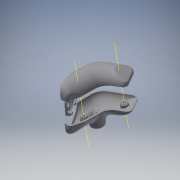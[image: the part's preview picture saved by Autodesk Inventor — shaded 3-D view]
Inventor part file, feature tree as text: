
AUTODESK INVENTOR PART (.ipt)
format: ipt  version: 2016 (Build 200138000, 138)  size: 18,297,344 bytes
history: native  units: in
note: dims shown in document units (in); Inventor stores cm internally (conversion verified against a paired STEP export)
features: sketch x44, other x39, extrude x33, surface_op x32, fillet x22, draft x19, plane x18, chamfer x18, move_body x12, projected_geometry x10, loft x4, shell x4, boolean_combine x2, split x2, delete_face x1
ambient origin geometry x8: Origin, YZ Plane, XZ Plane, XY Plane, X Axis, Y Axis, Z Axis, Center Point
bodies: Solid1 (feature_tree), Solid2 (feature_tree), Solid5 (feature_tree), Solid8 (feature_tree), Solid9 (feature_tree), Solid10 (feature_tree), Solid6 (feature_tree), Solid7 (feature_tree), Solid12 (feature_tree), Solid13 (feature_tree)
feature tree (260):
  sketch  "Sketch1"  dims[d0=0.7in d1=0.6in]
  plane  "Work Plane1"
  sketch  "Sketch2"  dims[d2=2.0in d3=0.73in]
  loft  "Loft1"
  plane  "Work Plane3"
  plane  "Work Plane4"
  plane  "Work Plane6"
  delete_face  "Delete Face1"
  surface_op  "Extend1"
  sketch  "Sketch6"  dims[d4=0.68in d5=120.0deg d6=0.8125in d9=0.75in]
  surface_op  "Stitch Surface1"
  extrude  "Extrusion5"  Depth=2.0in
  extrude  "Extrusion6"  Depth=0.8125in TaperAngle=120.0deg
  boolean_combine  "Combine1"
  extrude  "Extrusion7"  TaperAngle=0.0deg  [1 undecoded]
  loft  "Loft5"
  fillet  "Fillet6"  Radius=1.0in
  fillet  "Fillet7"  Radius=0.1969in
  plane  "Work Plane7"
  plane  "Work Plane8"
  extrude  "Extrusion10"  Depth=0.1969in
  draft  "FaceDraft1"
  fillet  "Fillet15"  [1 undecoded]
  extrude  "Extrusion15"  TaperAngle=90.0deg  [1 undecoded]
  fillet  "Fillet19"  Radius=0.35in
  fillet  "Fillet20"  [1 undecoded]
  extrude  "Extrusion9"  Depth=0.1in
  fillet  "Fillet11"  Radius=0.0687in
  fillet  "Fillet22"  Radius=0.75in
  shell  "Shell1"  Thickness=0.875in
  extrude  "Extrusion16"  Depth=0.3937in
  extrude  "Extrusion11"  Depth=0.141in
  draft  "FaceDraft5"
  sketch  "3D Sketch2"
  plane  "Work Plane9"
  extrude  "Extrusion17"  Depth=0.3125in TaperAngle=0.0deg
  plane  "Work Plane10"
  extrude  "Extrusion18"  Depth=0.0172in
  plane  "Work Plane11"
  extrude  "Extrusion19"  Depth=0.225in
  plane  "Work Plane12"
  extrude  "Extrusion20"  Depth=0.13in
  draft  "FaceDraft2"
  draft  "FaceDraft3"
  extrude  "Extrusion21"  Depth=0.4in
  extrude  "Extrusion22"  [1 undecoded]
  sketch  "Sketch25"  dims[d130=-0.625in d131=0.4in]
  extrude  "Extrusion23"  Depth=1.0in TaperAngle=0.0deg
  extrude  "Extrusion24"  Depth=0.28in
  extrude  "Extrusion25"  [1 undecoded]
  draft  "FaceDraft4"
  extrude  "Extrusion26"  Depth=1.0in TaperAngle=0.0deg
  plane  "Work Plane13"
  sketch  "Sketch29"  dims[d140=1.0in d141=0.0in d142=-0.06in]
  plane  "Work Plane14"
  sketch  "Sketch30"  dims[d143=0.28in d144=1.0in d145=0.0in]
  surface_op  "Stitch Surface5"
  surface_op  "Extend3"
  surface_op  "Extend4"
  surface_op  "Stitch Surface6"
  sketch  "Sketch35"  dims[d151=0.13in d152=1.0in d153=0.0in]
  surface_op  "Stitch Surface7"
  split  "Split2"
  sketch  "Sketch39"  dims[d160=0.06in d161=1.0in d162=0.0in]
  extrude  "Extrusion27"  Depth=0.0206in
  chamfer  "Chamfer4"  Distance=1.0in
  chamfer  "Chamfer5"  Distance=1.0in
  chamfer  "Chamfer6"  Distance=1.0in
  chamfer  "Chamfer7"  Distance=1.0in
  chamfer  "Chamfer9"  Distance=1.0in
  chamfer  "Chamfer10"  Distance=1.0in
  chamfer  "Chamfer11"  Distance=0.1969in
  chamfer  "Chamfer16"  [1 undecoded]
  chamfer  "Chamfer17"  [1 undecoded]
  chamfer  "Chamfer12"  [1 undecoded]
  chamfer  "Chamfer18"  [1 undecoded]
  chamfer  "Chamfer19"  [1 undecoded]
  chamfer  "Chamfer20"  [1 undecoded]
  chamfer  "Chamfer21"  [1 undecoded]
  chamfer  "Chamfer22"  [1 undecoded]
  chamfer  "Chamfer23"  [1 undecoded]
  chamfer  "Chamfer24"  Distance=0.1969in
  chamfer  "Chamfer25"  [1 undecoded]
  extrude  "Extrusion29"  Depth=0.02in
  draft  "FaceDraft6"
  fillet  "Fillet26"  Radius=0.02in
  move_body  "Move Body2"
  move_body  "Move Body3"
  draft  "FaceDraft7"
  draft  "FaceDraft8"
  draft  "FaceDraft9"
  draft  "FaceDraft10"
  extrude  "Extrusion30"  TaperAngle=0.0deg  [1 undecoded]
  draft  "FaceDraft16"
  draft  "FaceDraft17"
  extrude  "Extrusion31"  Depth=0.1969in TaperAngle=0.0deg
  extrude  "Extrusion32"  TaperAngle=0.0deg  [1 undecoded]
  extrude  "Extrusion33"  Depth=0.1969in
  draft  "FaceDraft18"
  draft  "FaceDraft19"
  draft  "FaceDraft20"
  fillet  "Fillet28"  Radius=0.1969in
  extrude  "Extrusion34"  TaperAngle=0.0deg  [1 undecoded]
  extrude  "Extrusion35"  Depth=0.1969in
  extrude  "Extrusion36"  Depth=0.5in
  draft  "FaceDraft21"
  draft  "FaceDraft22"
  draft  "FaceDraft23"
  shell  "Shell2"  Thickness=0.35in
  shell  "Shell3"  Thickness=0.125in
  shell  "Shell4"  Thickness=0.05in
  fillet  "Fillet32"  Radius=0.05in
  fillet  "Fillet29"  Radius=0.05in
  fillet  "Fillet30"  Radius=0.05in
  fillet  "Fillet31"  Radius=0.05in
  fillet  "Fillet33"  Radius=0.05in
  extrude  "Extrusion40"  Depth=0.05in
  draft  "FaceDraft26"
  fillet  "Fillet44"  Radius=0.05in
  fillet  "Fillet39"  Radius=0.05in
  move_body  "Move Body4"
  fillet  "Fillet45"  Radius=0.05in
  fillet  "Fillet46"  Radius=0.05in
  fillet  "Fillet37"  Radius=0.05in
  fillet  "Fillet48"  Radius=0.05in
  fillet  "Fillet49"  Radius=0.05in
  fillet  "Fillet50"  Radius=0.05in
  sketch  "Sketch57"  dims[d172=0.0in]
  sketch  "Sketch60"  dims[d173=0.1969in]
  other  "Work Point1"
  other  "Work Point2"
  other  "Work Point3"
  plane  "Work Plane17"
  move_body  "Move Body5"
  move_body  "Move Body6"
  move_body  "Move Body7"
  move_body  "Move Body8"
  other  "Work Axis1"
  other  "Work Axis2"
  boolean_combine  "Combine2"
  split  "Split3"
  loft  "Loft6"
  loft  "Loft7"
  move_body  "Move Body10"
  move_body  "Move Body11"
  move_body  "Move Body12"
  move_body  "Move Body13"
  move_body  "Move Body14"
  sketch  "Sketch61"  dims[d174=0.0in]
  plane  "Work Plane18"
  extrude  "Extrusion46"  Depth=0.05in
  sketch  "3D Sketch3"
  plane  "Work Plane19"
  extrude  "Extrusion47"  Depth=0.05in
  sketch  "Sketch63"  dims[d176=0.1969in]
  plane  "Work Plane20"
  extrude  "Extrusion48"  Depth=0.0508in
  extrude  "Extrusion49"  Depth=0.05in
  extrude  "Extrusion50"  Depth=0.05in TaperAngle=0.0deg
  plane  "Work Plane2"
  plane  "Work Plane5"
  other  "Srf1"
  other  "Srf2"
  sketch  "Sketch8"  dims[d10=0.0in d11=90.0deg d12=0.0in d13=90.0deg]
  sketch  "Sketch9"  dims[d14=150.0deg d15=-0.5in d45=1.0in d46=0.0in d47=1.0in d48=0.0in d49=0.1969in]
  sketch  "Sketch11"  dims[d50=0.0in d51=0.1969in d52=0.0in]
  sketch  "Sketch12"  dims[d53=1.0in d54=0.0in d56=90.0deg d58=90.0deg]
  other  "Edges5"
  other  "Edges6"
  sketch  "Sketch13"  dims[d62=0.0in d63=90.0deg d64=0.0in d65=90.0deg d66=0.2875in d67=0.35in d78=90.0deg]
  sketch  "Sketch17"  dims[d79=1.0in d80=0.0in d81=0.1in d87=0.0687in d88=0.75in d89=0.875in d90=0.0in]
  sketch  "Sketch18"  dims[d92=0.3937in d93=0.3937in]
  projected_geometry  "Projected Loop3"
  other  "Silhouette Curve2"
  sketch  "Sketch19"  dims[d94=0.2625in d95=0.141in]
  sketch  "Sketch20"  dims[d96=0.5in d97=0.3125in d98=0.0in]
  sketch  "Sketch21"  dims[d107=0.1in d114=0.0172in]
  sketch  "Sketch22"  dims[d117=0.121in d118=0.0in]
  sketch  "Sketch23"  dims[d119=0.1in d120=0.1in d121=0.13in d122=0.1969in d123=0.3in d124=0.2169in d125=0.225in]
  sketch  "Sketch24"  dims[d126=0.15in d127=0.0in d129=0.13in]
  sketch  "Sketch26"  dims[d132=1.0in d133=0.0in d134=-0.875in]
  sketch  "Sketch27"  dims[d135=0.4in d136=1.0in d137=0.0in]
  sketch  "Sketch28"  dims[d138=-0.06in d139=0.28in]
  other  "Srf3"
  other  "Srf4"
  other  "Srf5"
  other  "Srf6"
  other  "Srf7"
  other  "Srf8"
  other  "Srf12"
  other  "Srf13"
  other  "Srf15"
  other  "Srf17"
  other  "Srf18"
  other  "Srf19"
  other  "Srf21"
  other  "Srf24"
  other  "Srf25"
  sketch  "Sketch33"  dims[d146=0.0206in d147=0.0206in]
  sketch  "Sketch34"  dims[d148=0.13in d149=1.0in d150=0.0in]
  other  "Srf28"
  other  "Srf30"
  other  "Srf31"
  other  "Srf32"
  other  "Srf33"
  other  "Srf34"
  other  "Srf35"
  sketch  "Sketch36"  dims[d154=0.06in]
  other  "Srf36"
  other  "Srf37"
  other  "Srf38"
  sketch  "Sketch37"  dims[d155=0.06in d156=1.0in d157=0.0in d158=1.0in d159=0.0in]
  sketch  "Sketch41"  dims[d163=0.0206in]
  sketch  "Sketch43"  dims[d164=0.23in d165=1.0in d166=0.0in]
  sketch  "Sketch44"  dims[d167=15.0deg]
  sketch  "Sketch45"  dims[d168=0.125in]
  sketch  "Sketch46"  dims[d169=0.125in]
  sketch  "Sketch47"  dims[d170=0.0in]
  projected_geometry  "Projected Loop4"
  projected_geometry  "Projected Loop5"
  sketch  "Sketch51"  dims[d171=0.1969in]
  projected_geometry  "Projected Loop13"
  other  "Edges7"
  other  "Edges8"
  other  "Edges9"
  other  "Edges10"
  projected_geometry  "Projected Loop14"
  sketch  "Sketch62"  dims[d175=0.0in]
  projected_geometry  "Projected Loop15"
  projected_geometry  "Projected Loop16"
  sketch  "Sketch65"  dims[d177=0.0in d178=0.1969in d179=0.0in]
  sketch  "Sketch66"  dims[d184=0.0in d185=0.0in d187=0.0in d191=0.0in d192=0.0in d193=0.0in d197=0.0in d201=0.0in d204=0.0in d208=0.0in d209=0.1969in d210=0.0in d212=0.02in d213=0.02in d214=0.0in d216=0.1969in d217=0.1969in d218=0.0in d219=0.0in d220=0.1969in d221=0.1969in d222=0.0in d223=0.1969in d227=0.5in d228=0.35in d229=0.125in d233=0.05in d234=0.05in d235=0.0in d236=0.05in d237=0.125in d238=0.1374in d239=0.05in d240=0.125in d241=0.1374in d242=0.05in d243=0.125in d244=0.1374in d245=0.05in d246=0.125in d247=0.1374in d251=0.05in d252=0.125in d253=0.0687in d254=0.05in d255=0.125in d256=0.0687in d257=0.05in d258=0.125in d259=0.0687in d260=0.05in d261=0.125in d262=0.0687in d272=0.05in d273=0.125in d274=0.0687in d275=0.05in d276=0.125in d277=0.0687in d278=0.05in d279=0.125in d280=0.0687in d281=0.05in d282=0.125in d283=0.0687in d284=0.05in d285=0.125in d286=0.0687in d287=0.05in d288=0.125in d289=0.0687in d290=0.05in d291=0.125in d292=0.0687in d293=0.05in d294=0.125in d295=0.0687in d296=0.05in d297=0.125in d298=0.0687in d299=0.0508in d300=0.125in d301=0.0687in d302=0.05in d308=0.05in d309=0.0in d310=0.1374in d311=0.03in d312=0.0in d313=1.0in d314=0.0in d315=0.0in d316=-1.0in d317=0.0in d318=0.0206in d319=0.0206in d320=0.0206in d321=0.0206in d323=0.2756in d324=0.3in d325=0.025in d326=1.0in d327=0.0in d337=0.0206in d338=0.0206in d340=0.45in d341=0.08in d342=0.4in d344=0.52in d345=0.0962in d346=0.05in d347=0.025in d349=0.09in d350=0.0in d351=0.008in d352=0.09in d353=0.0in d354=0.008in d355=0.09in d356=0.0in d357=0.0206in d358=0.0206in d359=0.0206in d360=0.015in d361=0.01in d362=0.01in d363=0.01in d365=0.025in d366=0.04in d367=0.0in d371=0.04in d372=0.0in d373=0.04in d374=0.04in d375=0.0in d376=0.01in d377=0.04in d378=0.008in d379=0.04in d380=0.025in d381=0.0206in d382=0.0206in d383=0.0206in d384=0.04in d385=0.04in d386=0.01in d399=0.05in d400=0.075in d401=0.221in d402=0.0in d403=0.05in d404=0.075in d405=0.488in d406=0.04in d407=0.38in d409=-0.5in d410=0.0in d411=0.0in d412=0.01in d431=0.02in d437=0.01in d438=0.005in d439=0.005in d441=0.004in d442=0.003in d443=0.003in d444=0.2909in d445=0.0033in d446=0.6025in d447=0.1425in d448=0.1769in d449=0.5879in d450=1.0588in d451=0.0385in d452=0.2953in d453=1.2533in d454=1.2286in d455=0.3856in d456=0.075in d457=0.0069in d458=0.0143in d462=-1.0in d463=0.0in d464=0.0in d465=-1.0in d466=0.0in d467=0.0in d468=-1.0in d469=0.0in d470=0.0in d471=-1.0in d472=0.0in d473=0.0in d477=0.0in d478=90.0deg d479=0.0in d480=90.0deg d481=0.0in d482=90.0deg d483=0.0in d484=90.0deg d485=-1.5in d486=1.0in d487=0.75in d488=0.0in d489=1.0in d490=0.75in d491=0.0in d492=1.0in d493=0.75in d494=0.0in d495=1.0in d496=0.75in d497=0.0in d498=15.0deg d499=1.0in d500=0.0in d501=1.0in d502=0.0in d503=-0.1374in d504=1.0in d505=0.0in d506=0.1in d507=0.0in d508=0.0in d509=0.1in d510=0.0in]
  projected_geometry  "Projected Loop17"
  surface_op  "Boundary Patch1"
  surface_op  "Boundary Patch2"
  projected_geometry  "Project Cut Edges1"
  projected_geometry  "Project Cut Edges2"
  surface_op  "Boundary Patch3"
  surface_op  "Boundary Patch4"
  surface_op  "Boundary Patch5"
  surface_op  "Boundary Patch6"
  surface_op  "Boundary Patch7"
  surface_op  "Boundary Patch8"
  surface_op  "Boundary Patch12"
  surface_op  "Boundary Patch13"
  surface_op  "Boundary Patch15"
  surface_op  "Boundary Patch17"
  surface_op  "Boundary Patch18"
  surface_op  "Boundary Patch19"
  surface_op  "Boundary Patch21"
  surface_op  "Boundary Patch23"
  surface_op  "Boundary Patch24"
  surface_op  "Boundary Patch26"
  surface_op  "Boundary Patch27"
  surface_op  "Boundary Patch28"
  surface_op  "Boundary Patch29"
  surface_op  "Boundary Patch30"
  surface_op  "Boundary Patch31"
  surface_op  "Boundary Patch32"
  surface_op  "Boundary Patch33"
note: 19 required parameter values undecoded (feature->parameter linkage not recoverable at this tier; creation-order binding heuristic only, values carry confidence <= 0.55)
